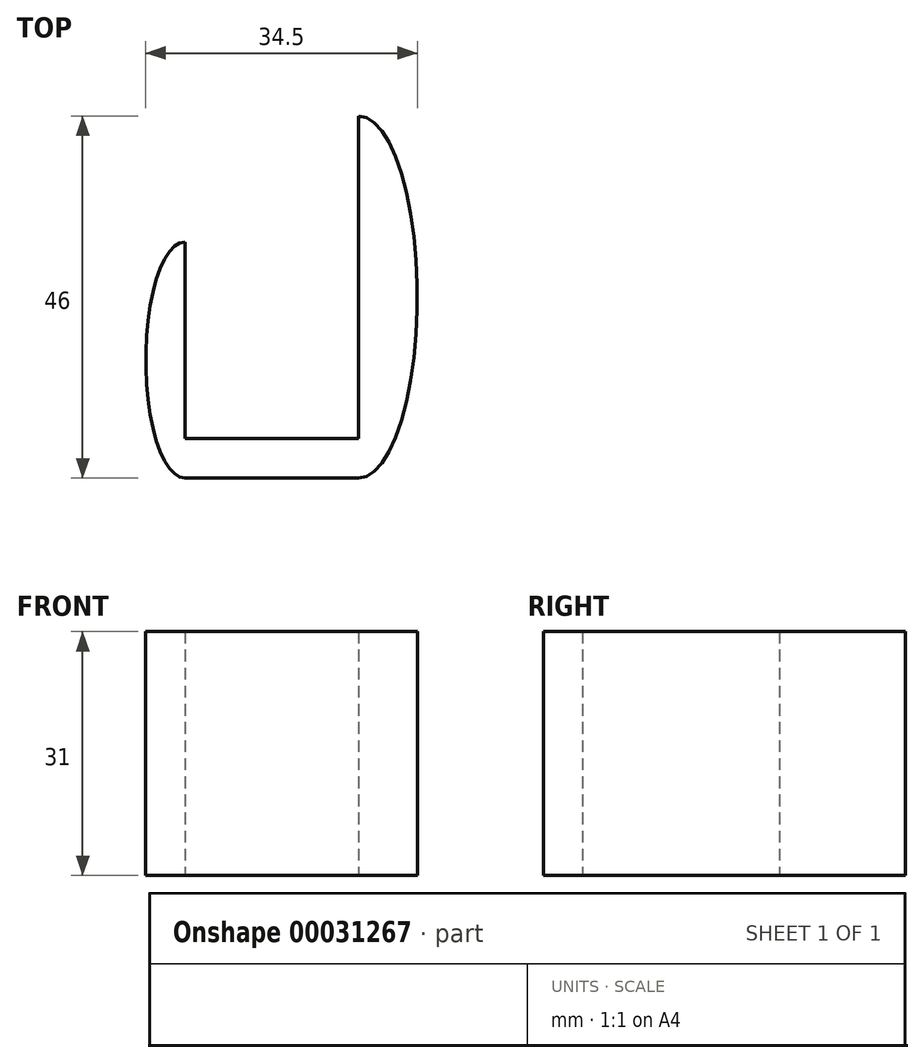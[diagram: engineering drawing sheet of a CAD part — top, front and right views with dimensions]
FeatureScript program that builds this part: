
annotation { "Feature Type Name" : "Feature", "Feature Type Description" : "" }
export const myFeature = defineFeature(function(context is Context, id is Id, definition is map)
    precondition{}
    {
        {
            var Q0;
            Q0=qCreatedBy(makeId("Top.planeOp"),FACE);
            var sketch = newSketch(context, id + "F0", { "sketchPlane" : qUnion([Q0])});
            skLineSegment(sketch, "E0.bottom", {"start": v(-11, 20.5) * mm, "end": v(11, 20.5) * mm, "construction": true});
            skLineSegment(sketch, "E0.top", {"start": v(-11, -20.5) * mm, "end": v(11, -20.5) * mm, "construction": true});
            skLineSegment(sketch, "E0.left", {"start": v(-11, 20.5) * mm, "end": v(-11, -20.5) * mm, "construction": true});
            skLineSegment(sketch, "E0.right", {"start": v(11, 20.5) * mm, "end": v(11, -20.5) * mm, "construction": true});
            skPoint(sketch, "E0.middle", {"position": v(0, 0) * mm});
            skEllipticalArc(sketch, "E1", {});
            skPoint(sketch, "E2", {"position": v(18.5, -2.5) * mm});
            skPoint(sketch, "E3", {"position": v(11, -25.5) * mm});
            skEllipticalArc(sketch, "E4", {});
            skPoint(sketch, "E5", {"position": v(-11, -25.5) * mm});
            skPoint(sketch, "E6", {"position": v(-16, -10.5) * mm});
            skLineSegment(sketch, "E7", {"start": v(-11, 4.5) * mm, "end": v(-11, -20.5) * mm});
            skLineSegment(sketch, "E8", {"start": v(11, -20.5) * mm, "end": v(-11, -20.5) * mm});
            skLineSegment(sketch, "E9", {"start": v(11, 20.5) * mm, "end": v(11, -20.5) * mm});
            skLineSegment(sketch, "E10", {"start": v(-11, -25.5) * mm, "end": v(11, -25.5) * mm});
            const initialGuessF0  = {"E1": [0.011, -0.0025, 0, 1, 0.023, 0.0075, 3.141592653589793, 0], "E4": [-0.011, -0.0105, 0, 1, 0.015, 0.005, 0, 3.141592653589793]};
            skSetInitialGuess(sketch, initialGuessF0);
            skSolve(sketch);
        }
        {
            var Q0;
            Q0 = qSketchRegion(id + "F0", true);
            extrude(context, id + "F1", {"entities" : qUnion([Q0]), "depth" : (31 / 2) * mm, "hasSecondDirection" : true, "secondDirectionOppositeDirection" : true, "secondDirectionDepth" : (31 / 2) * mm});
        }
    });
